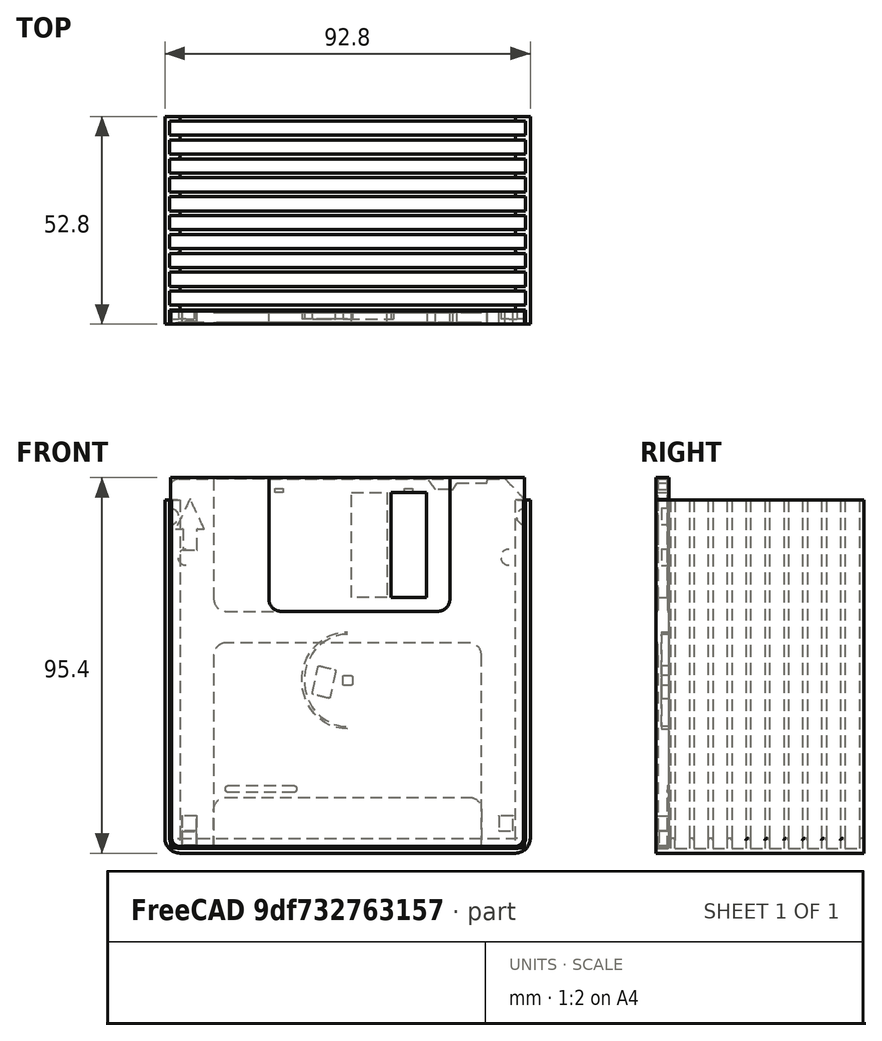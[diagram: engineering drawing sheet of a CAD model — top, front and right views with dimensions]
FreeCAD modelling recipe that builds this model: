
FCSTD DOCUMENT  (FreeCAD 1.0R39319 (Git))
Label: floppy_disk_coaster_Stand_02
License: CERN Open Hardware Licence permissive
LicenseURL: https://cern-ohl.web.cern.ch/
objects: Sketcher::SketchObject×4, PartDesign::Body×3, PartDesign::Pad×2, Part::FeaturePython×2, Part::Feature×1, PartDesign::AdditivePipe×1, PartDesign::LinearPattern×1, PartDesign::SubShapeBinder×1
note: 26 computed .brp shape members not serialized (recipe doc carries the construction recipe); baked Part::Feature solids carry a one-line shape summary decoded from their .brp

FEATURE [Sketcher::SketchObject] Sketch
  ArcFitTolerance = 1e-06
  AttachmentSupport = -> [XZ_Plane]
  FullyConstrained = true
  MakeInternals = false
  MapMode = 5
  Placement = pos=(0,0,0) rot=(1,0,0;1.5708rad)
  sketch-geometry (4):
    g0: LineSegment StartX=0 StartY=0 StartZ=0 EndX=90 EndY=0 EndZ=0
    g1: LineSegment StartX=90 StartY=0 StartZ=0 EndX=90 EndY=94 EndZ=0
    g2: LineSegment StartX=90 StartY=94 StartZ=0 EndX=0 EndY=94 EndZ=0
    g3: LineSegment StartX=0 StartY=94 StartZ=0 EndX=0 EndY=0 EndZ=0
  constraints (11):
    c: Coincident(g0,g1)
    c: Coincident(g1,g2)
    c: Coincident(g2,g3)
    c: Coincident(g3,g0)
    c: Horizontal(g0)
    c: Horizontal(g2)
    c: Vertical(g1)
    c: Vertical(g3)
    c: Coincident(g0,g-1)
    c: DistanceX(g0,g0) = 90
    c: Distance(g1,g1) = 94
FEATURE [PartDesign::Pad] Pad
  Direction = (0,-1,2e-16)
  Length = 3.3
  Length2 = 10
  Placement = pos=(0,0,0) rot=(1,0,0;1.5708rad)
  Profile = -> Sketch
  ReferenceAxis = -> Sketch [N_Axis]
  Refine = true
  Reversed = true
  Suppressed = false
  Type = 0
FEATURE [PartDesign::Body] Body
  AllowCompound = false
  Group = -> [Sketch,Pad]
  Origin = -> Origin
  Tip = -> Pad
FEATURE [Part::Feature] Part__Feature  label="Disket 01"
  shape: bbox 451.6 x 10.2 x 442 mm, 273 faces, 4 solids (baked)
FEATURE [Part::FeaturePython] Clone  label="Disket 002"  # Draft clone (typed FeaturePython)
  AttacherType = Attacher::AttachEngine3D
  Fuse = false
  Objects = -> [Part__Feature]
  Placement = pos=(90,1.96,92.1317) rot=(0,0,1;3.14159rad)
  Scale = (0.2,0.2,0.2)
FEATURE [Part::FeaturePython] Clone001  label="Disket 003"  # Draft clone (typed FeaturePython)
  AttacherType = Attacher::AttachEngine3D
  Fuse = false
  Objects = -> [Clone]
  Placement = pos=(90,3.3,98.1202) rot=(0,0,1;3.14159rad)
  Scale = (1,1.65,1.065)
FEATURE [Sketcher::SketchObject] Sketch002
  ArcFitTolerance = 1e-06
  AttachmentOffset = pos=(0,0,88.3) rot=(0,0,1;0rad)
  AttachmentSupport = -> [XY_Plane001]
  FullyConstrained = true
  MakeInternals = false
  MapMode = 5
  Placement = pos=(0,0,88.3) rot=(0,0,1;0rad)
  sketch-geometry (6):
    g0: LineSegment StartX=-0.2 StartY=0 StartZ=0 EndX=-0.2 EndY=3.6 EndZ=0
    g1: LineSegment StartX=-0.2 StartY=3.6 StartZ=0 EndX=1.8 EndY=3.6 EndZ=0
    g2: ArcOfCircle CenterX=1.8 CenterY=4.2 CenterZ=0 NormalX=0 NormalY=0 NormalZ=1 AngleXU=0 Radius=0.6 StartAngle=4.71239 EndAngle=7.85398
    g3: LineSegment StartX=1.8 StartY=4.8 StartZ=0 EndX=-1.4 EndY=4.8 EndZ=0
    g4: LineSegment StartX=-1.4 StartY=4.8 StartZ=0 EndX=-1.4 EndY=0 EndZ=0
    g5: LineSegment StartX=-1.4 StartY=0 StartZ=0 EndX=-0.2 EndY=0 EndZ=0
  constraints (18):
    c: PointOnObject(g0,g-1)
    c: Vertical(g0)
    c: Coincident(g0,g1)
    c: Horizontal(g1)
    c: Tangent(g1,g2) = -1.5708
    c: Horizontal(g3)
    c: Coincident(g3,g4)
    c: PointOnObject(g4,g-1)
    c: Vertical(g4)
    c: Coincident(g4,g5)
    c: Coincident(g5,g0)
    c: Tangent(g2,g3) = -1.5708
    c: DistanceX(g0,g-1) = 0.2
    c: DistanceX(g5,g5) = 1.2
    c: Radius(g2) = 0.6
    c: DistanceY(g0,g0) = 3.6
    c: DistanceX(g1,g1) = 2
    c: DistanceY(g4,g4) = 4.8
FEATURE [Sketcher::SketchObject] Sketch001
  ArcFitTolerance = 1e-06
  AttachmentSupport = -> [XZ_Plane001]
  ExternalGeometry = -> [Sketch002]
  FullyConstrained = true
  MakeInternals = false
  MapMode = 5
  Placement = pos=(0,0,0) rot=(1,0,0;1.5708rad)
  sketch-geometry (13):
    g0: LineSegment [constr] StartX=7.683e-13 StartY=90 StartZ=0 EndX=7.683e-13 EndY=2 EndZ=0
    g1: LineSegment [constr] StartX=2 StartY=0 StartZ=0 EndX=88 EndY=0 EndZ=0
    g2: LineSegment [constr] StartX=90 StartY=2 StartZ=0 EndX=90 EndY=90 EndZ=0
    g3: ArcOfCircle [constr] CenterX=2 CenterY=2 CenterZ=0 NormalX=0 NormalY=0 NormalZ=1 AngleXU=0 Radius=2 StartAngle=3.14159 EndAngle=4.71239
    g4: GeomPoint [constr] X=0 Y=0 Z=0
    g5: ArcOfCircle [constr] CenterX=88 CenterY=2 CenterZ=0 NormalX=0 NormalY=0 NormalZ=1 AngleXU=0 Radius=2 StartAngle=4.71239 EndAngle=6.28319
    g6: GeomPoint [constr] X=90 Y=0 Z=0
    g7: LineSegment StartX=2.4 StartY=88.3 StartZ=0 EndX=2.4 EndY=2.4 EndZ=0
    g8: LineSegment StartX=2.4 StartY=2.4 StartZ=0 EndX=87.6 EndY=2.4 EndZ=0
    g9: LineSegment StartX=87.6 StartY=2.4 StartZ=0 EndX=87.6 EndY=88.3 EndZ=0
    g10: LineSegment [constr] StartX=2.4 StartY=88.3 StartZ=0 EndX=0 EndY=88.3 EndZ=0
    g11: LineSegment [constr] StartX=2.4 StartY=2.4 StartZ=0 EndX=2.4 EndY=0 EndZ=0
    g12: LineSegment [constr] StartX=87.6 StartY=2.4 StartZ=0 EndX=90 EndY=2.4 EndZ=0
  constraints (36):
    c: Vertical(g0)
    c: Horizontal(g1)
    c: Vertical(g2)
    c: DistanceY(g4,g0) = 90
    c: DistanceX(g4,g6) = 90
    c: Coincident(g4,g-1)
    c: PointOnObject(g4,g0)
    c: PointOnObject(g4,g1)
    c: Tangent(g0,g3) = -1.5708
    c: Tangent(g1,g3) = -1.5708
    c: PointOnObject(g6,g2)
    c: PointOnObject(g6,g1)
    c: Tangent(g2,g5) = -1.5708
    c: Tangent(g1,g5) = -1.5708
    c: Equal(g5,g3)
    c: Equal(g2,g0)
    c: Radius(g3) = 2
    c: Coincident(g7,g-3)
    c: Vertical(g7)
    c: Coincident(g8,g7)
    c: Horizontal(g8)
    c: Coincident(g9,g8)
    c: Vertical(g9)
    c: Equal(g9,g7)
    c: Distance(g7,g0) = 2.4
    c: Coincident(g10,g7)
    c: PointOnObject(g10,g0)
    c: Horizontal(g10)
    c: Coincident(g11,g7)
    c: PointOnObject(g11,g1)
    c: Vertical(g11)
    c: Coincident(g12,g8)
    c: PointOnObject(g12,g2)
    c: Horizontal(g12)
    c: Equal(g12,g11)
    c: Equal(g11,g10)
FEATURE [PartDesign::AdditivePipe] AdditivePipe
  AuxilleryCurvelinear = true
  AuxillerySpineTangent = false
  Binormal = (0,0,0)
  Mode = 0
  Profile = -> Sketch002
  Refine = true
  Spine = -> Sketch001 [Edge1,Edge2,Edge3]
  SpineTangent = false
  Suppressed = false
  Transformation = 0
  Transition = 2
FEATURE [PartDesign::LinearPattern] LinearPattern
  BaseFeature = -> AdditivePipe
  Direction = -> Sketch002 [V_Axis]
  Length = 48
  Mode = 0
  Occurrences = 11
  Offset = 4.8
  Originals = -> [AdditivePipe]
  Refine = true
  Suppressed = false
  TransformMode = 0
FEATURE [PartDesign::Body] Body001
  AllowCompound = false
  Group = -> [Sketch001,Sketch002,AdditivePipe,LinearPattern]
  Origin = -> Origin001
  Tip = -> LinearPattern
FEATURE [PartDesign::SubShapeBinder] Binder
  BindCopyOnChange = 0
  BindMode = 0
  ClaimChildren = false
  Context = -> Body002 [Binder.]
  Fuse = false
  MakeFace = true
  OffsetFill = false
  OffsetIntersection = false
  OffsetJoinType = 0
  OffsetOpenResult = false
  PartialLoad = false
  Refine = true
  Relative = true
  Support = -> [Body001]
  _Version = 2
FEATURE [Sketcher::SketchObject] Sketch003
  ArcFitTolerance = 1e-06
  AttachmentSupport = -> [Binder]
  ExternalGeometry = -> [Binder]
  FullyConstrained = true
  MakeInternals = false
  MapMode = 5
  Placement = pos=(0,3.6,0) rot=(1,0,0;1.5708rad)
  sketch-geometry (12):
    g0: LineSegment StartX=-0.2 StartY=88.3 StartZ=0 EndX=-0.2 EndY=2.4 EndZ=0
    g1: ArcOfCircle CenterX=2.4 CenterY=2.4 CenterZ=0 NormalX=0 NormalY=0 NormalZ=1 AngleXU=0 Radius=2.6 StartAngle=3.14159 EndAngle=4.71239
    g2: LineSegment StartX=2.4 StartY=-0.2 StartZ=0 EndX=87.6 EndY=-0.2 EndZ=0
    g3: ArcOfCircle CenterX=87.6 CenterY=2.4 CenterZ=0 NormalX=0 NormalY=0 NormalZ=1 AngleXU=0 Radius=2.6 StartAngle=4.71239 EndAngle=6.28319
    g4: LineSegment StartX=90.2 StartY=2.4 StartZ=0 EndX=90.2 EndY=88.3 EndZ=0
    g5: LineSegment StartX=90.2 StartY=88.3 StartZ=0 EndX=89.7 EndY=88.3 EndZ=0
    g6: LineSegment StartX=89.7 StartY=88.3 StartZ=0 EndX=89.7 EndY=2.4 EndZ=0
    g7: ArcOfCircle CenterX=87.6 CenterY=2.4 CenterZ=0 NormalX=0 NormalY=0 NormalZ=1 AngleXU=0 Radius=2.1 StartAngle=4.71239 EndAngle=6.28319
    g8: LineSegment StartX=87.6 StartY=0.3 StartZ=0 EndX=2.4 EndY=0.3 EndZ=0
    g9: ArcOfCircle CenterX=2.4 CenterY=2.4 CenterZ=0 NormalX=0 NormalY=0 NormalZ=1 AngleXU=0 Radius=2.1 StartAngle=3.14159 EndAngle=4.71239
    g10: LineSegment StartX=0.3 StartY=2.4 StartZ=0 EndX=0.3 EndY=88.3 EndZ=0
    g11: LineSegment StartX=0.3 StartY=88.3 StartZ=0 EndX=-0.2 EndY=88.3 EndZ=0
  constraints (26):
    c: Coincident(g-3,g0)
    c: Coincident(g0,g-4)
    c: Tangent(g0,g1) = -1.5708
    c: Coincident(g1,g-5)
    c: Coincident(g1,g2)
    c: Coincident(g2,g-6)
    c: Tangent(g2,g3) = -1.5708
    c: Coincident(g4,g-7)
    c: Coincident(g4,g5)
    c: Horizontal(g5)
    c: Coincident(g5,g6)
    c: Vertical(g6)
    c: Tangent(g6,g7) = 1.5708
    c: Horizontal(g8)
    c: Tangent(g8,g9) = 1.5708
    c: Vertical(g10)
    c: Coincident(g10,g11)
    c: Coincident(g11,g0)
    c: Horizontal(g11)
    c: Coincident(g1,g9)
    c: Coincident(g3,g7)
    c: Tangent(g7,g8) = 1.5708
    c: Tangent(g3,g4) = -1.5708
    c: Tangent(g9,g10) = 1.5708
    c: DistanceX(g11,g11) = 0.5
    c: Vertical(g4)
FEATURE [PartDesign::Pad] Pad001
  Direction = (0,-1,2e-16)
  Length = 10
  Length2 = 10
  Profile = -> Sketch003
  ReferenceAxis = -> Sketch003 [N_Axis]
  Refine = true
  Suppressed = false
  Type = 3
  UpToFace = -> Binder [Face5]
FEATURE [PartDesign::Body] Body002
  AllowCompound = false
  Group = -> [Binder,Sketch003,Pad001]
  Origin = -> Origin002
  Tip = -> Pad001
